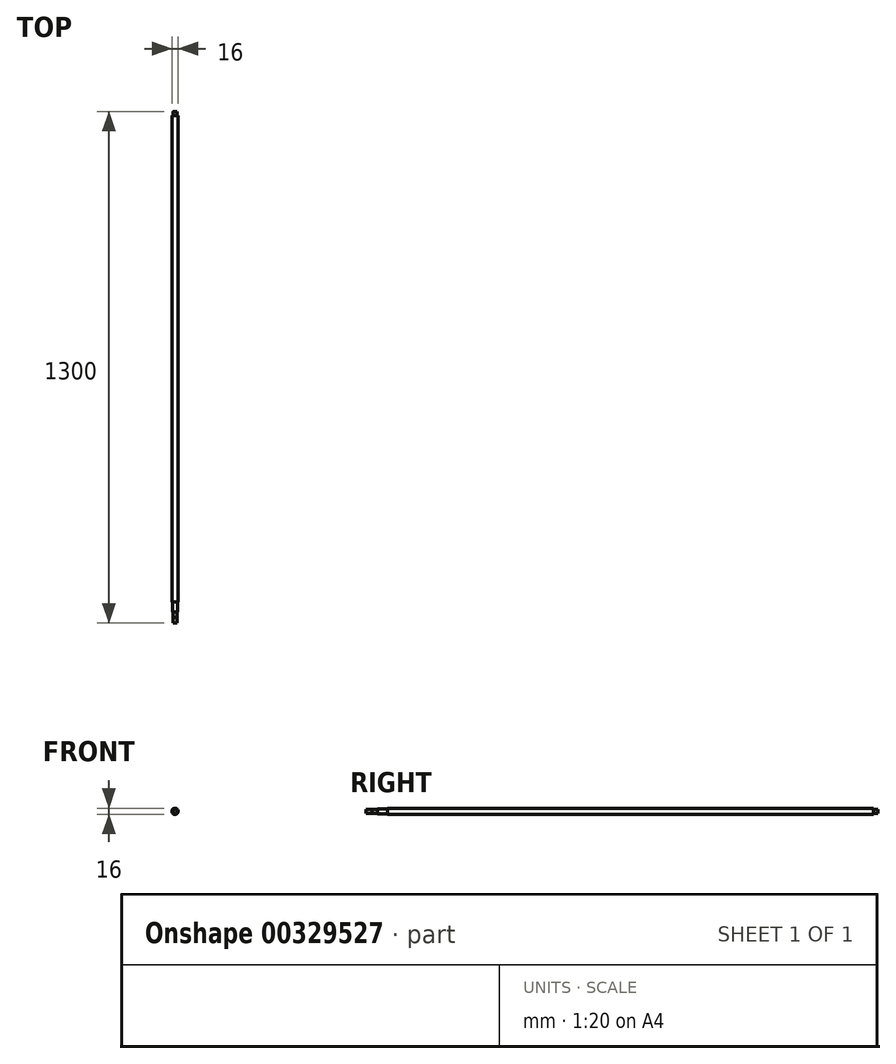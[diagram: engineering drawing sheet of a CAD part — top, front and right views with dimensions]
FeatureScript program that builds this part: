
annotation { "Feature Type Name" : "Feature", "Feature Type Description" : "" }
export const myFeature = defineFeature(function(context is Context, id is Id, definition is map)
    precondition{}
    {
        {
            var Q0;
            Q0=qCreatedBy(makeId("Front.planeOp"),FACE);
            var sketch = newSketch(context, id + "F0", { "sketchPlane" : qUnion([Q0])});
            skCircle(sketch, "E0", {"center": v(0, 0) * mm, "radius": 8 * mm});
            skSolve(sketch);
        }
        {
            var Q0;
            Q0 = qSketchRegion(id + "F0", true);
            extrude(context, id + "F1", {"entities" : qUnion([Q0]), "endBound" : BoundingType.SYMMETRIC, "depth" : 1300 * mm});
        }
        {
            var Q0;
            Q0=makeQuery(id+"F1.opExtrude","CAP_FACE",FACE,{"disambiguationData":[OSD([sQuery(id+"F0.wireOp",EDGE,"E0")])],"isStart":false});
            var sketch = newSketch(context, id + "F2", { "sketchPlane" : qUnion([Q0])});
            skCircle(sketch, "E1", {"center": v(0, 0) * mm, "radius": 6 * mm});
            skCircle(sketch, "E2", {"center": v(0, 0) * mm, "radius": 8 * mm});
            skSolve(sketch);
        }
        {
            var Q0;
            Q0 = qSketchRegion(id + "F2", true);
            extrude(context, id + "F3", {"entities" : qUnion([Q0]), "operationType" : NewBodyOperationType.REMOVE, "oppositeDirection" : true, "depth" : 54 * mm});
        }
        {
            var Q0;
            Q0=makeQuery(id+"F1.opExtrude","CAP_FACE",FACE,{"disambiguationData":[OSD([sQuery(id+"F0.wireOp",EDGE,"E0")])],"isStart":false});
            var sketch = newSketch(context, id + "F4", { "sketchPlane" : qUnion([Q0])});
            skCircle(sketch, "E3", {"center": v(0, 0) * mm, "radius": 6 * mm});
            skCircle(sketch, "E4", {"center": v(0, 0) * mm, "radius": 5.15 * mm});
            skSolve(sketch);
        }
        {
            var Q0;
            Q0 = qSketchRegion(id + "F4", true);
            extrude(context, id + "F5", {"entities" : qUnion([Q0]), "operationType" : NewBodyOperationType.REMOVE, "oppositeDirection" : true, "depth" : 29 * mm});
        }
        {
            var Q0;
            Q0=makeQuery(id+"F1.opExtrude","CAP_FACE",FACE,{"disambiguationData":[OSD([sQuery(id+"F0.wireOp",EDGE,"E0")])],"isStart":false});
            var sketch = newSketch(context, id + "F6", { "sketchPlane" : qUnion([Q0])});
            skCircle(sketch, "E5", {"center": v(0, 0) * mm, "radius": 5 * mm});
            skCircle(sketch, "E6", {"center": v(0, 0) * mm, "radius": 5.15 * mm});
            skSolve(sketch);
        }
        {
            var Q0;
            Q0 = qSketchRegion(id + "F6", true);
            extrude(context, id + "F7", {"entities" : qUnion([Q0]), "operationType" : NewBodyOperationType.REMOVE, "oppositeDirection" : true, "depth" : 15 * mm});
        }
        {
            var Q0;
            Q0=makeQuery(id+"F1.opExtrude","CAP_FACE",FACE,{"disambiguationData":[OSD([sQuery(id+"F0.wireOp",EDGE,"E0")])],"isStart":true});
            var sketch = newSketch(context, id + "F8", { "sketchPlane" : qUnion([Q0])});
            skCircle(sketch, "E7", {"center": v(0, 0) * mm, "radius": 8 * mm});
            skCircle(sketch, "E8", {"center": v(0, 0) * mm, "radius": 5 * mm});
            skSolve(sketch);
        }
        {
            var Q0;
            Q0 = qSketchRegion(id + "F8", true);
            extrude(context, id + "F9", {"entities" : qUnion([Q0]), "operationType" : NewBodyOperationType.REMOVE, "oppositeDirection" : true, "depth" : 11 * mm});
        }
    });
